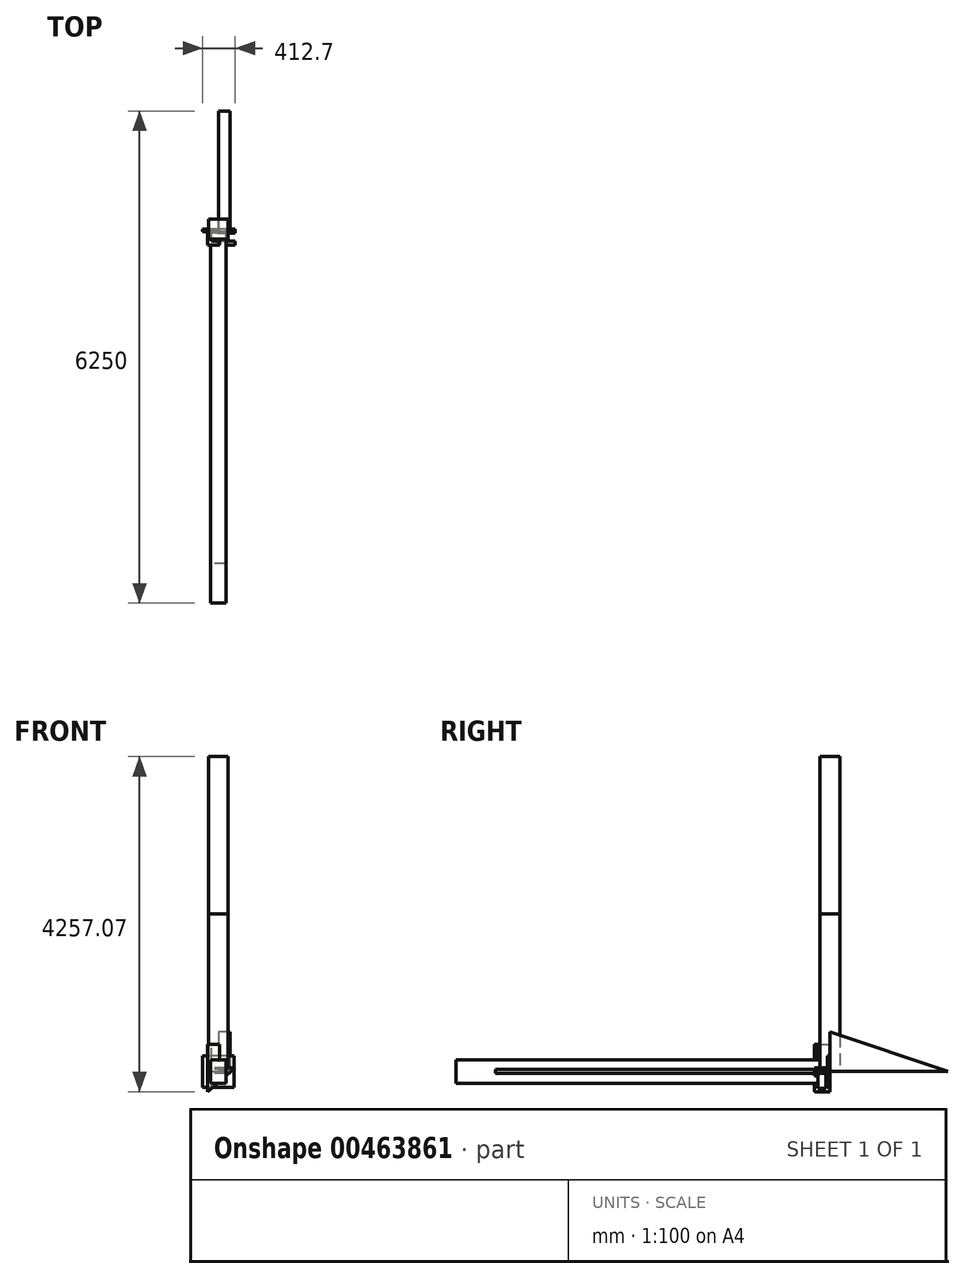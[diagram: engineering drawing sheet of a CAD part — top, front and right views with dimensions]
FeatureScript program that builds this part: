
annotation { "Feature Type Name" : "Feature", "Feature Type Description" : "" }
export const myFeature = defineFeature(function(context is Context, id is Id, definition is map)
    precondition{}
    {
        {
            var Q0;
            Q0=qCreatedBy(makeId("Top.planeOp"),FACE);
            var sketch = newSketch(context, id + "F0", { "sketchPlane" : qUnion([Q0])});
            skLineSegment(sketch, "E0.bottom", {"start": v(125, -125) * mm, "end": v(-125, -125) * mm});
            skLineSegment(sketch, "E0.top", {"start": v(125, 125) * mm, "end": v(-125, 125) * mm});
            skLineSegment(sketch, "E0.left", {"start": v(125, -125) * mm, "end": v(125, 125) * mm});
            skLineSegment(sketch, "E0.right", {"start": v(-125, -125) * mm, "end": v(-125, 125) * mm});
            skPoint(sketch, "E0.middle", {"position": v(0, 0) * mm});
            skSolve(sketch);
        }
        {
            var Q0;
            Q0=makeQuery(id+"F0.imprint","IMPRINT",FACE,{"disambiguationData":[TD([[makeQuery(id+"F0.imprint","IMPRINT",EDGE,{"derivedFrom":sQuery(id+"F0.wireOp",EDGE,"E0.bottom")}),-1.0]])]});
            extrude(context, id + "F1", {"entities" : qUnion([Q0]), "depth" : 4000 * mm});
        }
        {
            var Q0;
            Q0=qCreatedBy(makeId("Top.planeOp"),FACE);
            var sketch = newSketch(context, id + "F2", { "sketchPlane" : qUnion([Q0])});
            skLineSegment(sketch, "E1.bottom", {"start": v(100, -25) * mm, "end": v(-100, -25) * mm});
            skLineSegment(sketch, "E1.top", {"start": v(100, 25) * mm, "end": v(-100, 25) * mm});
            skLineSegment(sketch, "E1.left", {"start": v(100, -25) * mm, "end": v(100, 25) * mm});
            skLineSegment(sketch, "E1.right", {"start": v(-100, -25) * mm, "end": v(-100, 25) * mm});
            skPoint(sketch, "E1.middle", {"position": v(0, 0) * mm});
            skSolve(sketch);
        }
        {
            var Q0;
            Q0=makeQuery(id+"F2.imprint","IMPRINT",FACE,{"disambiguationData":[TD([[makeQuery(id+"F2.imprint","IMPRINT",EDGE,{"derivedFrom":sQuery(id+"F2.wireOp",EDGE,"E1.bottom")}),-1.0]])]});
            extrude(context, id + "F3", {"entities" : qUnion([Q0]), "depth" : 3500 * mm});
        }
        {
            var Q0;
            Q0=qCreatedBy(makeId("Front.planeOp"),FACE);
            var sketch = newSketch(context, id + "F4", { "sketchPlane" : qUnion([Q0])});
            skLineSegment(sketch, "E2.bottom", {"start": v(100, -150) * mm, "end": v(-100, -150) * mm});
            skLineSegment(sketch, "E2.top", {"start": v(100, 150) * mm, "end": v(-100, 150) * mm});
            skLineSegment(sketch, "E2.left", {"start": v(100, -150) * mm, "end": v(100, 150) * mm});
            skLineSegment(sketch, "E2.right", {"start": v(-100, -150) * mm, "end": v(-100, 150) * mm});
            skPoint(sketch, "E2.middle", {"position": v(0, 0) * mm});
            skSolve(sketch);
        }
        {
            var Q0;
            Q0=makeQuery(id+"F4.imprint","IMPRINT",FACE,{"disambiguationData":[TD([[makeQuery(id+"F4.imprint","IMPRINT",EDGE,{"derivedFrom":sQuery(id+"F4.wireOp",EDGE,"E2.bottom")}),-1.0]])]});
            extrude(context, id + "F5", {"entities" : qUnion([Q0]), "depth" : 4750 * mm});
        }
        {
            var Q0;
            Q0=qCreatedBy(makeId("Front.planeOp"),FACE);
            var sketch = newSketch(context, id + "F6", { "sketchPlane" : qUnion([Q0])});
            skLineSegment(sketch, "E3", {"start": v(-137.3, 42.93) * mm, "end": v(-137.3, -257.07) * mm});
            skLineSegment(sketch, "E4", {"start": v(-137.3, -257.07) * mm, "end": v(-137.3, -257.07) * mm});
            skLineSegment(sketch, "E5", {"start": v(-137.3, -257.07) * mm, "end": v(212.7, 42.93) * mm});
            skLineSegment(sketch, "E6", {"start": v(212.7, 42.93) * mm, "end": v(-137.3, 42.93) * mm});
            skSolve(sketch);
        }
        {
            var Q0;
            Q0=makeQuery(id+"F6.imprint","IMPRINT",FACE,{"disambiguationData":[TD([[makeQuery(id+"F6.imprint","IMPRINT",EDGE,{"derivedFrom":sQuery(id+"F6.wireOp",EDGE,"E3")}),1.0]])]});
            extrude(context, id + "F7", {"entities" : qUnion([Q0]), "depth" : 200 * mm});
        }
        {
            var Q0;
            Q0=makeQuery(id+"F7.opExtrude","SWEPT_FACE",FACE,{"disambiguationData":[OSD([sQuery(id+"F6.wireOp",EDGE,"E6")])]});
            var sketch = newSketch(context, id + "F8", { "sketchPlane" : qUnion([Q0])});
            skLineSegment(sketch, "E7.bottom", {"start": v(212.7, -150) * mm, "end": v(-87.3, -150) * mm});
            skLineSegment(sketch, "E7.top", {"start": v(212.7, -50) * mm, "end": v(-87.3, -50) * mm});
            skLineSegment(sketch, "E7.left", {"start": v(212.7, -150) * mm, "end": v(212.7, -50) * mm});
            skLineSegment(sketch, "E7.right", {"start": v(-87.3, -150) * mm, "end": v(-87.3, -50) * mm});
            skSolve(sketch);
        }
        {
            var Q0;
            Q0=makeQuery(id+"F8.imprint","IMPRINT",FACE,{"disambiguationData":[TD([[makeQuery(id+"F8.imprint","IMPRINT",EDGE,{"derivedFrom":sQuery(id+"F8.wireOp",EDGE,"E7.bottom")}),-1.0]])]});
            extrude(context, id + "F9", {"entities" : qUnion([Q0]), "operationType" : NewBodyOperationType.REMOVE, "endBound" : BoundingType.THROUGH_ALL, "oppositeDirection" : true, "depth" : 25 * mm});
        }
        {
            var Q0;
            Q0=qCreatedBy(makeId("Front.planeOp"),FACE);
            var sketch = newSketch(context, id + "F10", { "sketchPlane" : qUnion([Q0])});
            skLineSegment(sketch, "E8.bottom", {"start": v(100, -25) * mm, "end": v(-100, -25) * mm});
            skLineSegment(sketch, "E8.top", {"start": v(100, 25) * mm, "end": v(-100, 25) * mm});
            skLineSegment(sketch, "E8.left", {"start": v(100, -25) * mm, "end": v(100, 25) * mm});
            skLineSegment(sketch, "E8.right", {"start": v(-100, -25) * mm, "end": v(-100, 25) * mm});
            skPoint(sketch, "E8.middle", {"position": v(0, 0) * mm});
            skSolve(sketch);
        }
        {
            var Q0;
            Q0=makeQuery(id+"F10.imprint","IMPRINT",FACE,{"disambiguationData":[TD([[makeQuery(id+"F10.imprint","IMPRINT",EDGE,{"derivedFrom":sQuery(id+"F10.wireOp",EDGE,"E8.bottom")}),-1.0]])]});
            extrude(context, id + "F11", {"entities" : qUnion([Q0]), "depth" : 4250 * mm});
        }
        {
            var Q0;
            Q0=makeQuery(id+"F7.opExtrude","SWEPT_FACE",FACE,{"disambiguationData":[OSD([sQuery(id+"F6.wireOp",EDGE,"E6")])]});
            var sketch = newSketch(context, id + "F12", { "sketchPlane" : qUnion([Q0])});
            skLineSegment(sketch, "E9.bottom", {"start": v(-137.3, 0) * mm, "end": v(12.7, 0) * mm});
            skLineSegment(sketch, "E9.top", {"start": v(-137.3, -200) * mm, "end": v(12.7, -200) * mm});
            skLineSegment(sketch, "E9.left", {"start": v(-137.3, 0) * mm, "end": v(-137.3, -200) * mm});
            skLineSegment(sketch, "E9.right", {"start": v(12.7, 0) * mm, "end": v(12.7, -200) * mm});
            skSolve(sketch);
        }
        {
            var Q0;
            {var subQ1=sQuery(id+"F12.wireOp",EDGE,"E9.bottom");Q0=makeQuery(id+"F12.imprint","IMPRINT",FACE,{"disambiguationData":[TD([[makeQuery(id+"F12.imprint","IMPRINT",EDGE,{"derivedFrom":subQ1}),1.0]])]});}
            var Q1;
            {var subQ5=makeQuery(id+"F9.boolean.opBoolean","COPY",EDGE,{"derivedFrom":makeQuery(id+"F9.opExtrude","CAP_EDGE",EDGE,{"disambiguationData":[OSD([sQuery(id+"F8.wireOp",EDGE,"E7.right")])],"isStart":true})});Q1=makeQuery(id+"F12.imprint","IMPRINT",FACE,{"disambiguationData":[TD([[makeQuery(id+"F12.imprint","IMPRINT",EDGE,{"derivedFrom":subQ5}),-1.0]])]});}
            extrude(context, id + "F13", {"entities" : qUnion([Q0, Q1]), "operationType" : NewBodyOperationType.ADD, "depth" : 300 * mm});
        }
        {
            var Q0;
            Q0=qCreatedBy(makeId("Front.planeOp"),FACE);
            var sketch = newSketch(context, id + "F14", { "sketchPlane" : qUnion([Q0])});
            skLineSegment(sketch, "E10.bottom", {"start": v(200, -200) * mm, "end": v(-200, -200) * mm});
            skLineSegment(sketch, "E10.top", {"start": v(200, 200) * mm, "end": v(-200, 200) * mm});
            skLineSegment(sketch, "E10.left", {"start": v(200, -200) * mm, "end": v(200, 200) * mm});
            skLineSegment(sketch, "E10.right", {"start": v(-200, -200) * mm, "end": v(-200, 200) * mm});
            skPoint(sketch, "E10.middle", {"position": v(0, 0) * mm});
            skSolve(sketch);
        }
        {
            var Q0;
            Q0=makeQuery(id+"F14.imprint","IMPRINT",FACE,{"disambiguationData":[TD([[makeQuery(id+"F14.imprint","IMPRINT",EDGE,{"derivedFrom":sQuery(id+"F14.wireOp",EDGE,"E10.bottom")}),-1.0]])]});
            extrude(context, id + "F15", {"entities" : qUnion([Q0]), "depth" : 30 * mm});
        }
        {
            var Q0;
            Q0=qCreatedBy(makeId("Right.planeOp"),FACE);
            var sketch = newSketch(context, id + "F16", { "sketchPlane" : qUnion([Q0])});
            skLineSegment(sketch, "E11", {"start": v(0, 0) * mm, "end": v(1500, 0) * mm});
            skLineSegment(sketch, "E12", {"start": v(1500, 0) * mm, "end": v(0, 500) * mm});
            skLineSegment(sketch, "E13", {"start": v(0, 500) * mm, "end": v(0, 0) * mm});
            skSolve(sketch);
        }
        {
            var Q0;
            Q0=makeQuery(id+"F16.imprint","IMPRINT",FACE,{"disambiguationData":[TD([[makeQuery(id+"F16.imprint","IMPRINT",EDGE,{"derivedFrom":sQuery(id+"F16.wireOp",EDGE,"E11")}),1.0]])]});
            extrude(context, id + "F17", {"entities" : qUnion([Q0]), "depth" : 150 * mm});
        }
        {
            var Q0;
            Q0=qCreatedBy(makeId("Top.planeOp"),FACE);
            var sketch = newSketch(context, id + "F18", { "sketchPlane" : qUnion([Q0])});
            skLineSegment(sketch, "E14.bottom", {"start": v(-125, -125) * mm, "end": v(125, -125) * mm});
            skLineSegment(sketch, "E14.top", {"start": v(-125, 125) * mm, "end": v(125, 125) * mm});
            skLineSegment(sketch, "E14.left", {"start": v(-125, -125) * mm, "end": v(-125, 125) * mm});
            skLineSegment(sketch, "E14.right", {"start": v(125, -125) * mm, "end": v(125, 125) * mm});
            skPoint(sketch, "E14.middle", {"position": v(0, 0) * mm});
            skSolve(sketch);
        }
        {
            var Q0;
            Q0=makeQuery(id+"F18.imprint","IMPRINT",FACE,{"disambiguationData":[TD([[makeQuery(id+"F18.imprint","IMPRINT",EDGE,{"derivedFrom":sQuery(id+"F18.wireOp",EDGE,"E14.bottom")}),1.0]])]});
            extrude(context, id + "F19", {"entities" : qUnion([Q0]), "depth" : 2000 * mm});
        }
    });
